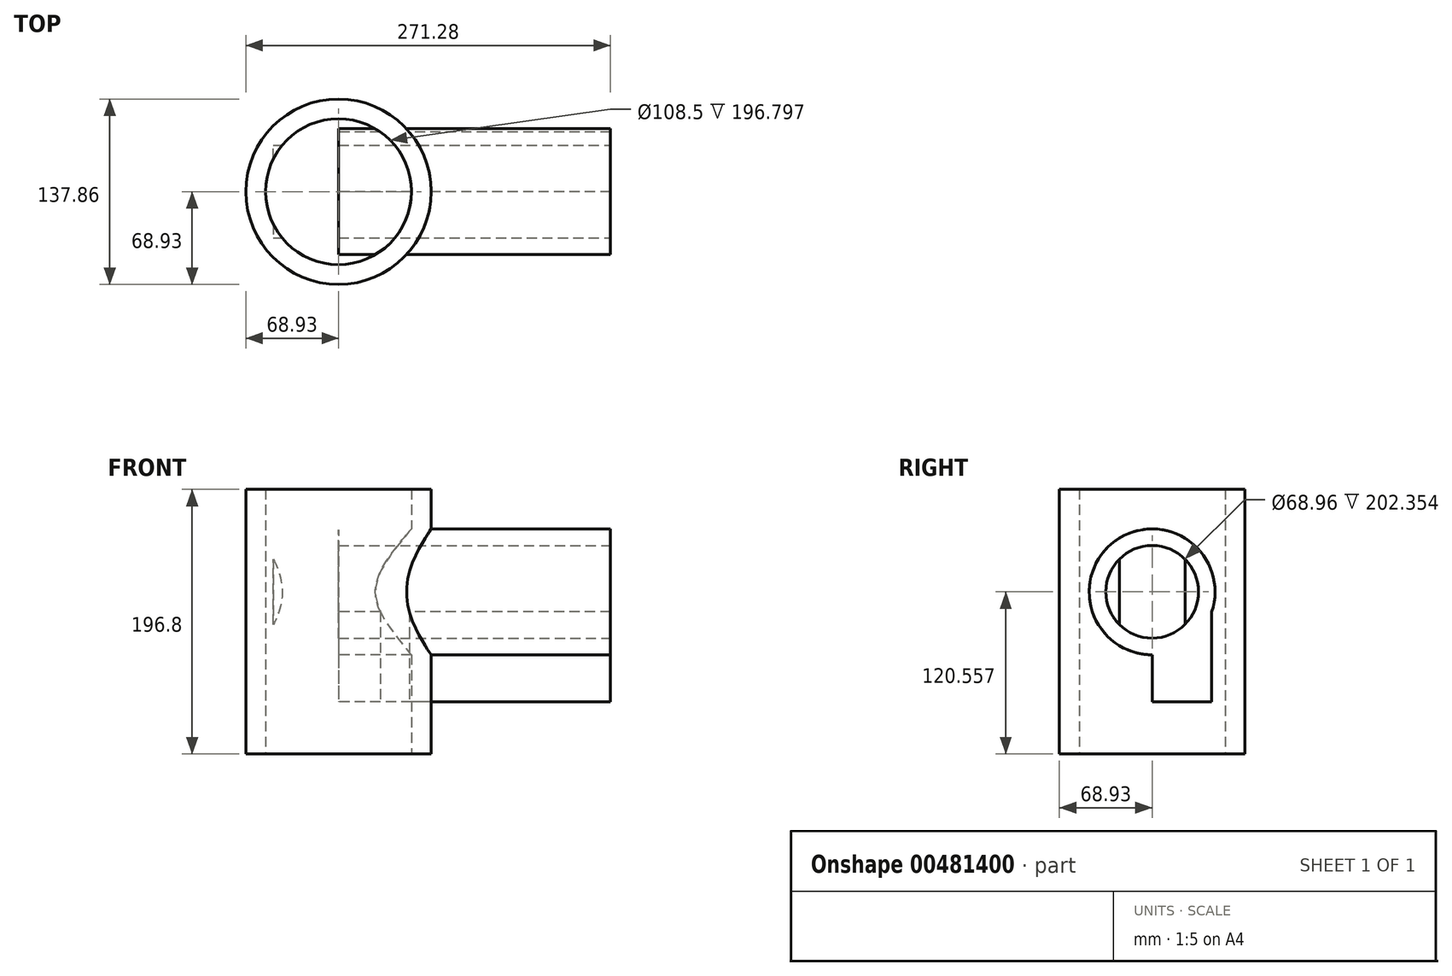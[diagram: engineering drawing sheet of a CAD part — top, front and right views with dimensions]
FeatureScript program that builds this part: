
annotation { "Feature Type Name" : "Feature", "Feature Type Description" : "" }
export const myFeature = defineFeature(function(context is Context, id is Id, definition is map)
    precondition{}
    {
        {
            var Q0;
            Q0=qCreatedBy(makeId("Top.planeOp"),FACE);
            var sketch = newSketch(context, id + "F0", { "sketchPlane" : qUnion([Q0])});
            skCircle(sketch, "E0", {"center": v(0, 0) * mm, "radius": 54.25 * mm});
            skCircle(sketch, "E1", {"center": v(0, 0) * mm, "radius": 68.93 * mm});
            skSolve(sketch);
        }
        {
            var Q0;
            Q0 = qSketchRegion(id + "F0", true);
            extrude(context, id + "F1", {"entities" : qUnion([Q0]), "depth" : 196.8 * mm});
        }
        {
            var Q0;
            Q0=qCreatedBy(makeId("Right.planeOp"),FACE);
            var sketch = newSketch(context, id + "F2", { "sketchPlane" : qUnion([Q0])});
            skLineSegment(sketch, "E2.bottom", {"start": v(0, 120.56) * mm, "end": v(44.4, 120.56) * mm});
            skLineSegment(sketch, "E2.top", {"start": v(0, 38.81) * mm, "end": v(44.4, 38.81) * mm});
            skLineSegment(sketch, "E2.left", {"start": v(0, 120.56) * mm, "end": v(0, 38.81) * mm});
            skLineSegment(sketch, "E2.right", {"start": v(44.4, 120.56) * mm, "end": v(44.4, 38.81) * mm});
            skCircle(sketch, "E3", {"center": v(0, 120.56) * mm, "radius": 46.81 * mm});
            skSolve(sketch);
        }
        {
            var Q0;
            Q0 = qSketchRegion(id + "F2", true);
            extrude(context, id + "F3", {"entities" : qUnion([Q0]), "operationType" : NewBodyOperationType.ADD, "depth" : 202.35 * mm});
        }
        {
            var Q0;
            Q0=makeQuery(id+"F3.opExtrude","CAP_FACE",FACE,{"disambiguationData":[OSD([sQuery(id+"F2.wireOp",EDGE,"E2.top"),sQuery(id+"F2.wireOp",EDGE,"E2.left"),sQuery(id+"F2.wireOp",EDGE,"E2.right"),sQuery(id+"F2.wireOp",EDGE,"E3")])],"isStart":false});
            var sketch = newSketch(context, id + "F4", { "sketchPlane" : qUnion([Q0])});
            skCircle(sketch, "E4", {"center": v(0, 120.56) * mm, "radius": 34.48 * mm});
            skSolve(sketch);
        }
        {
            var Q0;
            Q0 = qSketchRegion(id + "F4", true);
            extrude(context, id + "F5", {"entities" : qUnion([Q0]), "operationType" : NewBodyOperationType.REMOVE, "oppositeDirection" : true, "depth" : 250.79 * mm});
        }
    });
